# Revit family: VL414712
name_source: partatom
category: Generic Models
revit_build: Autodesk Revit Architecture 2016 (Build: 20150220_1215(x64)
units: mm (PartAtom-declared; Revit-internal decimal feet)

## family parameters
Can host rebar = No
Cut with Voids When Loaded = No
Host = Face
Part Type = Normal
Room Calculation Point = No
Round Connector Dimension = Use Diameter
Shared = No

## types (1)
- VL414712
    Default Elevation = 0 mm  [stored 0 ft]
    Depth = 155 mm
    Description = Gaggenau Vario downdraft ventilation 400 series stainless steel Width 15.5 cm Air extraction / Air recirculation Motorless
    Height = 175 mm
    Manufacturer = Gaggenau
    Model = VL414712
    URL = http://www.gaggenau.com.
    Unit = Metal Panel
    Width = 520 mm  [stored 1.70604 ft]

note: [stored X ft] marks values corroborated as IEEE doubles in the binary element streams (Revit-internal decimal feet)

## geometry (parser evidence)
native form markers: Sweep x2
no freeform markers — native parametric forms only
